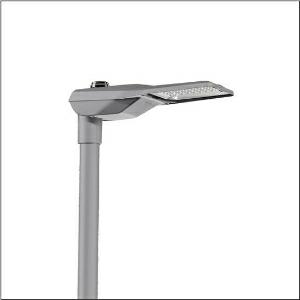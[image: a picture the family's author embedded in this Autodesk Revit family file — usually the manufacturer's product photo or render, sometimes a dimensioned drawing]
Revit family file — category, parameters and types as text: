
# Revit family: streetlight_sl_21_mini___st1_0a_5xe6d47n08hb_a00d
name_source: partatom
category: Lighting Fixtures
units: mm (PartAtom-declared; Revit-internal decimal feet)

## family parameters
Cut with Voids When Loaded = No
Host = Face
Light Source = No
Part Type = Normal
Room Calculation Point = No
Round Connector Dimension = Use Diameter
Shared = No

## types (1)
- --- (1 x LED, 9430 lm, 66 W, 4000K)
    Apparent Load = 66 VA
    CIE Flux Codes = 37 72 97 100 100
    Color Rendering = 70
    Color Temperature = 4000K
    Default Elevation = 1800 mm
    Description = Streetlight SL 21 mini, mast luminaire, primary light control with lens, of PMMA, primary optical cover: cover, of toughened safety glass, transparent, light distribution: ST1.0a, light emission: direct distribution, primary light characteristic: asymmetric, installation type: side-entry, LED, 3G 1.5mm², High Power LED, rated luminous flux: 9.430lm, luminous efficacy: 143lm/W, light colour: 740, colour temperature: 4000K, control gear: NEMA (7pin), control: overheat protection, pre-setting: linear dimming characteristic, constant luminous flux control, time-dependent luminous flux control, flexible luminous flux parameterisation, mains connection: 230..240V, AC, 50/60Hz, connection cable pre-assembled, cable length: 8,5m, wiring characteristics: H07RN-F, start of lifetime: 66W, end of service life: 69W, reduction: 30W, luminaire housing, of diecast aluminium (EN AC-44300), powder-coated, Siteco® metallic grey (DB 702S), corrosivity category C5 mid according to DIN EN ISO 12944, multi-level sealing system, sealing non-destructively replaceable, inclination adjustable: 0°, 5°, 10°, 15°, length: 628mm, width: 235mm, height: 110mm, spigot size: 42mm (side-entry), mounting height: 4..8m, protection rating (complete): IP66, insulation class (complete): insulation class I (protective earthing), certification: CE, ENEC, ENEC+, VDE, impact resistance: IK10, permissible operating ambient temperature for outdoor applications: -40..+50°C, standard-compliant lighting for roads and squares, packaging unit: 1 piece

Light Distribution: ST1.0a
    Height = 110 mm
    Lamp = 1 x LED
    Lamp Light Flux = 9430 lm
    Lamp Power = 66 W
    Lamp count = 1
    Length = 625 mm
    Luminous efficacy = 143 lm/W
    Manufacturer = Siteco
    ModVariant = No
    Model = 5XE6D47N08HB
    Number of Poles = 1
    OnlyDefault = Yes
    Power Factor = 1
    Product Name = Streetlight SL 21 mini | ST1.0a
    Product group = mast luminaire | pylon top
    ProductGroupID = 6100
    Protection Class = Protection class I
    Protection Degree = IP 66
    RLX_Detail_Level = 1
    RLX_Emergency_Light_Flux = 0 lm
    RLX_Emergency_Type = 0
    RLX_Emergency_Type_DB = No
    RlxData = <blob elided: 26177 chars, md5=d5bf0058>
    Socket = socket
    Standby Power = 0 W
    System Light Flux = 9430 lm
    System Power = 66 W
    Type Comments = factory setting: luminous flux: 100 % | dim-lin: 254 | 670 mA
    Type Image = l_1294379.jpg
    URL = http://relux.com
    VarID = @adj_136204
    Voltage = 0 V
    Weight = 0.00 kg
    Width = 234 mm

## geometry (parser evidence)
native form markers: Blend x4, Sweep x10
no freeform markers — native parametric forms only
